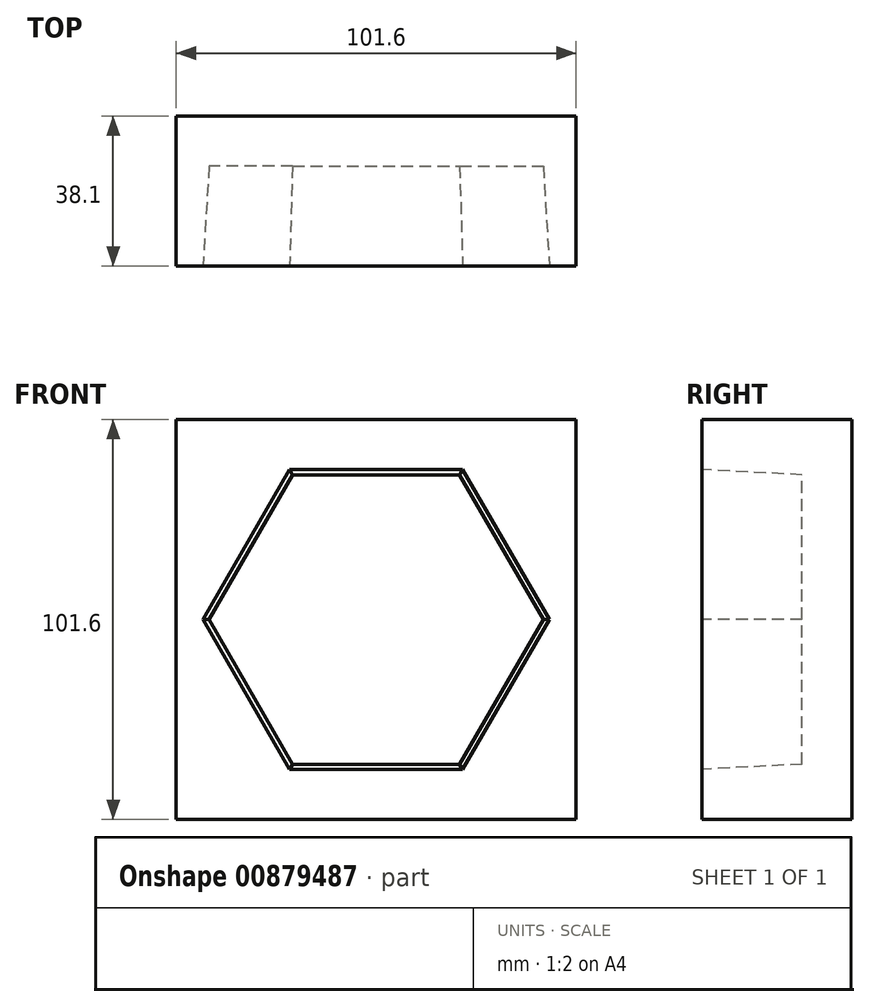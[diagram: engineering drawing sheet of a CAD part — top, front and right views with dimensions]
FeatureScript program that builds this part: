
annotation { "Feature Type Name" : "Feature", "Feature Type Description" : "" }
export const myFeature = defineFeature(function(context is Context, id is Id, definition is map)
    precondition{}
    {
        {
            var Q0;
            Q0=qCreatedBy(makeId("Front.planeOp"),FACE);
            var sketch = newSketch(context, id + "F0", { "sketchPlane" : qUnion([Q0])});
            skLineSegment(sketch, "E0.bottom", {"start": v(0, 0) * mm, "end": v(101.6, 0) * mm});
            skLineSegment(sketch, "E0.top", {"start": v(0, 101.6) * mm, "end": v(101.6, 101.6) * mm});
            skLineSegment(sketch, "E0.left", {"start": v(0, 0) * mm, "end": v(0, 101.6) * mm});
            skLineSegment(sketch, "E0.right", {"start": v(101.6, 0) * mm, "end": v(101.6, 101.6) * mm});
            skSolve(sketch);
        }
        {
            var Q0;
            Q0 = qSketchRegion(id + "F0", true);
            extrude(context, id + "F1", {"entities" : qUnion([Q0]), "depth" : 38.1 * mm, "offsetDistance" : 25.4 * mm});
        }
        {
            var Q0;
            Q0=makeQuery(id+"F1.opExtrude","CAP_FACE",FACE,{"disambiguationData":[OSD([sQuery(id+"F0.wireOp",EDGE,"E0.bottom"),sQuery(id+"F0.wireOp",EDGE,"E0.top"),sQuery(id+"F0.wireOp",EDGE,"E0.left"),sQuery(id+"F0.wireOp",EDGE,"E0.right")])],"isStart":false});
            var sketch = newSketch(context, id + "F2", { "sketchPlane" : qUnion([Q0])});
            skCircle(sketch, "E1.cCircle", {"center": v(50.8, 50.8) * mm, "radius": 38.1 * mm, "construction": true});
            skLineSegment(sketch, "E1.0", {"start": v(72.8, 12.7) * mm, "end": v(28.8, 12.7) * mm});
            skLineSegment(sketch, "E1.1", {"start": v(28.8, 12.7) * mm, "end": v(6.8, 50.8) * mm});
            skLineSegment(sketch, "E1.2", {"start": v(6.8, 50.8) * mm, "end": v(28.8, 88.9) * mm});
            skLineSegment(sketch, "E1.3", {"start": v(28.8, 88.9) * mm, "end": v(72.8, 88.9) * mm});
            skLineSegment(sketch, "E1.4", {"start": v(72.8, 88.9) * mm, "end": v(94.8, 50.8) * mm});
            skLineSegment(sketch, "E1.5", {"start": v(94.8, 50.8) * mm, "end": v(72.8, 12.7) * mm});
            skPoint(sketch, "E1.0.midPoint", {"position": v(50.8, 12.7) * mm});
            skLineSegment(sketch, "E2", {"start": v(50.8, 101.6) * mm, "end": v(50.8, 0) * mm, "construction": true});
            skSolve(sketch);
        }
        {
            var Q0;
            Q0 = qSketchRegion(id + "F2", true);
            extrude(context, id + "F3", {"entities" : qUnion([Q0]), "operationType" : NewBodyOperationType.REMOVE, "oppositeDirection" : true, "depth" : 25.4 * mm, "offsetDistance" : 25.4 * mm, "hasDraft" : true, "draftAngle" : 3 * degree, "draftPullDirection" : true});
        }
    });
